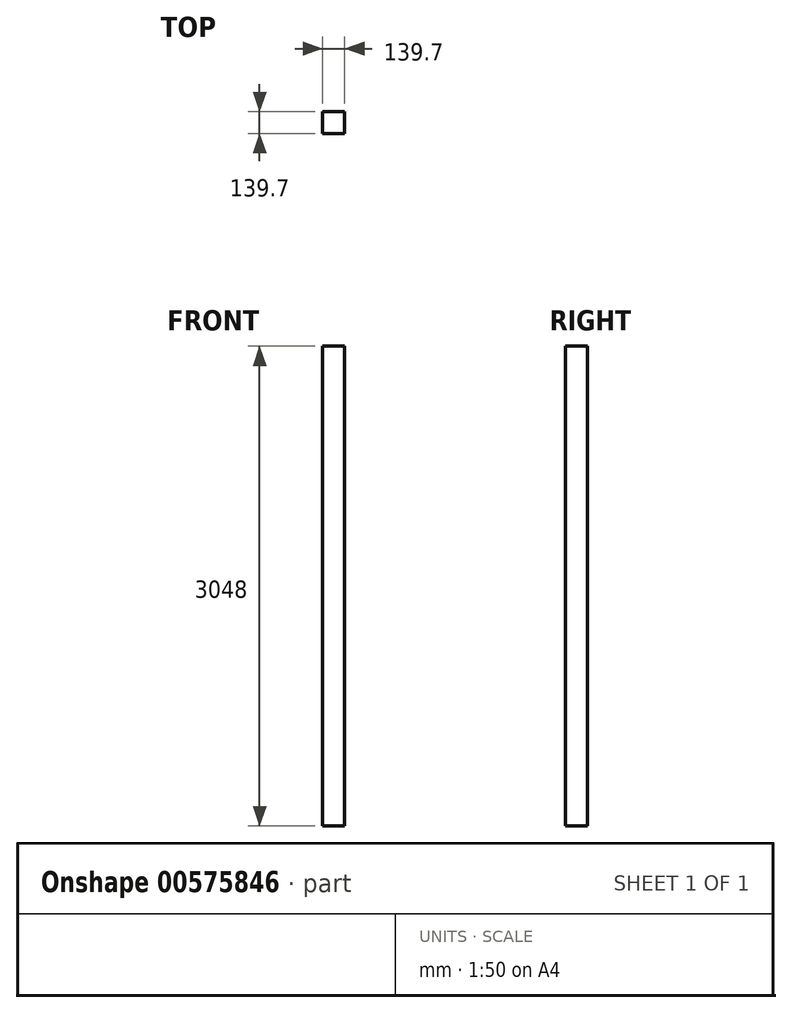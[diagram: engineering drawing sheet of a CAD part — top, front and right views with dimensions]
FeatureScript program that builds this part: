
annotation { "Feature Type Name" : "Feature", "Feature Type Description" : "" }
export const myFeature = defineFeature(function(context is Context, id is Id, definition is map)
    precondition{}
    {
        {
            var Q0;
            Q0=qCreatedBy(makeId("Top.planeOp"),FACE);
            var sketch = newSketch(context, id + "F0", { "sketchPlane" : qUnion([Q0])});
            skLineSegment(sketch, "E0.bottom", {"start": v(0, 0) * mm, "end": v(139.7, 0) * mm});
            skLineSegment(sketch, "E0.top", {"start": v(0, 139.7) * mm, "end": v(139.7, 139.7) * mm});
            skLineSegment(sketch, "E0.left", {"start": v(0, 0) * mm, "end": v(0, 139.7) * mm});
            skLineSegment(sketch, "E0.right", {"start": v(139.7, 0) * mm, "end": v(139.7, 139.7) * mm});
            skSolve(sketch);
        }
        {
            var Q0;
            Q0 = qSketchRegion(id + "F0", true);
            extrude(context, id + "F1", {"entities" : qUnion([Q0]), "depth" : 3048 * mm, "offsetDistance" : 25.4 * mm});
        }
    });
